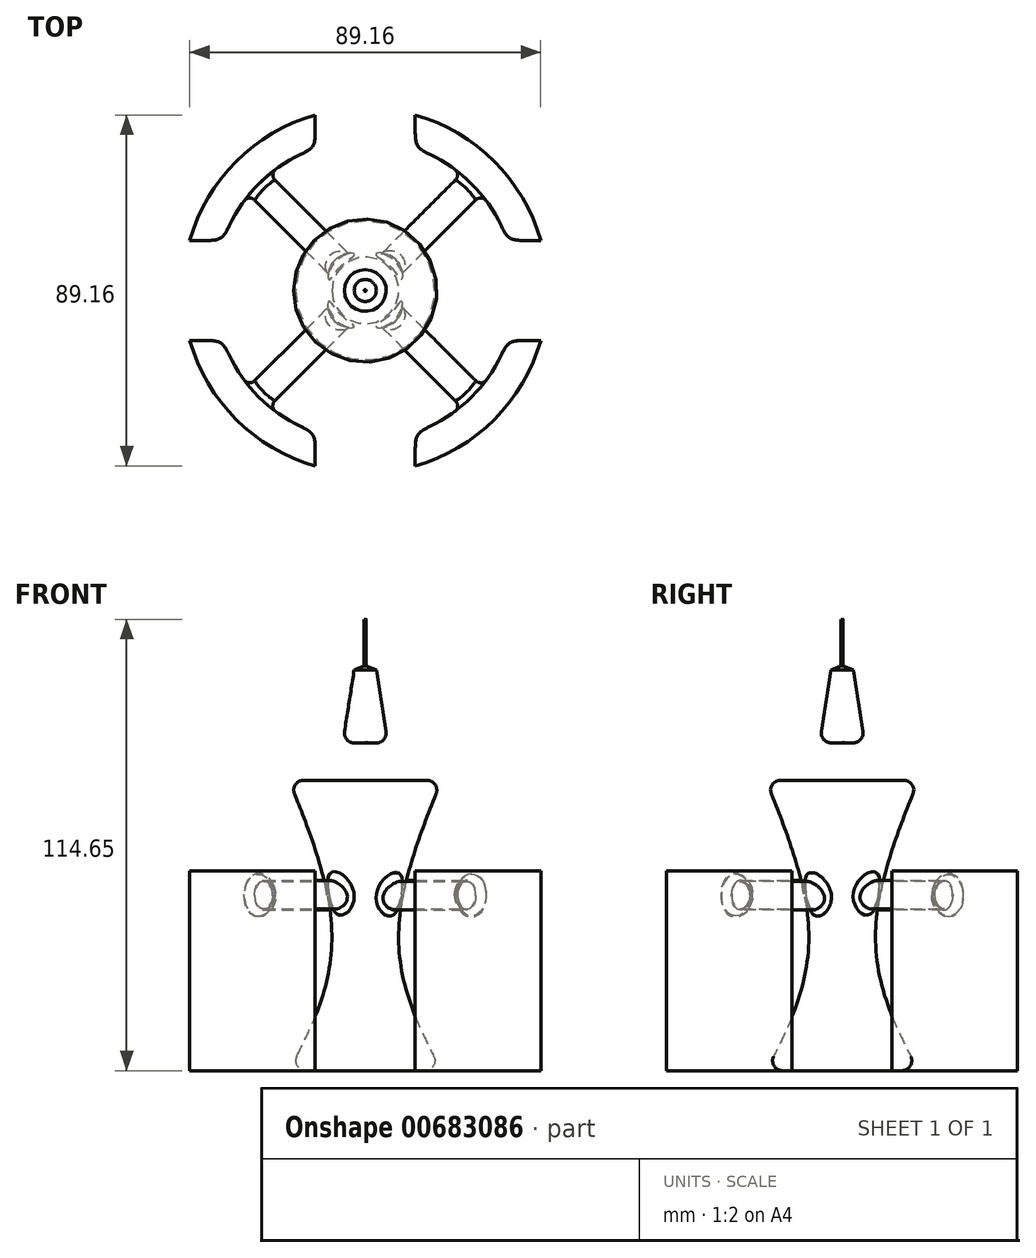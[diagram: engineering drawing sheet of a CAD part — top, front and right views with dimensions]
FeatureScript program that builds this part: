
annotation { "Feature Type Name" : "Feature", "Feature Type Description" : "" }
export const myFeature = defineFeature(function(context is Context, id is Id, definition is map)
    precondition{}
    {
        {
            var Q0;
            Q0=qCreatedBy(makeId("Front.planeOp"),FACE);
            var sketch = newSketch(context, id + "F0", { "sketchPlane" : qUnion([Q0])});
            skLineSegment(sketch, "E0", {"start": v(0, 0) * mm, "end": v(0, 83.5) * mm});
            skLineSegment(sketch, "E1", {"start": v(0, 0) * mm, "end": v(19.3, 0) * mm});
            skFitSpline(sketch, "E2", {"points": [v(19.3, 0) * mm, v(8.76, 39.22) * mm, v(19.3, 73.63) * mm, v(19.3, 73.81) * mm], "startDerivative": vector(-36.92, 71.14) * mm, "endDerivative": vector(-1.25, 3) * mm});
            skFitSpline(sketch, "E3", {"points": [v(19.32, 73.78) * mm, v(0, 83.5) * mm], "startDerivative": vector(-8.92, 8.43) * mm, "endDerivative": vector(-32.32, 1.43) * mm});
            skLineSegment(sketch, "E4", {"start": v(5.85, 82.58) * mm, "end": v(2.8, 101.8) * mm});
            skLineSegment(sketch, "E5", {"start": v(2.8, 101.8) * mm, "end": v(0.25, 102.86) * mm});
            skLineSegment(sketch, "E6", {"start": v(0, 102.96) * mm, "end": v(0, 83.5) * mm});
            skLineSegment(sketch, "E7", {"start": v(0, 102.96) * mm, "end": v(0, 114.65) * mm});
            skLineSegment(sketch, "E8.0", {"start": v(0.25, 102.86) * mm, "end": v(0.25, 114.65) * mm});
            skLineSegment(sketch, "E9", {"start": v(0.25, 114.65) * mm, "end": v(0, 114.65) * mm});
            skLineSegment(sketch, "E10", {"start": v(19.32, 73.78) * mm, "end": v(0, 73.78) * mm});
            skSolve(sketch);
        }
        {
            var Q0;
            {var subQ0=sQuery(id+"F0.wireOp",EDGE,"E0");Q0=makeQuery(id+"F0.imprint","IMPRINT",FACE,{"disambiguationData":[TD([[makeQuery(id+"F0.imprint","IMPRINT",EDGE,{"derivedFrom":subQ0}),-1.0]])]});}
            var Q1;
            {var subQ6=sQuery(id+"F0.wireOp",EDGE,"E6");Q1=makeQuery(id+"F0.imprint","IMPRINT",FACE,{"disambiguationData":[TD([[makeQuery(id+"F0.imprint","IMPRINT",EDGE,{"derivedFrom":subQ6}),1.0]])]});}
            var Q2;
            {var subQ0=sQuery(id+"F0.wireOp",EDGE,"E7");Q2=makeQuery(id+"F0.imprint","IMPRINT",FACE,{"disambiguationData":[TD([[makeQuery(id+"F0.imprint","IMPRINT",EDGE,{"derivedFrom":subQ0}),-1.0]])]});}
            var Q3;
            Q3=sQuery(id+"F0.wireOp",EDGE,"E7");
            revolve(context, id + "F1", {"entities" : qUnion([Q0, Q1, Q2]), "axis" : qUnion([Q3]), "revolveType" : RevolveType.FULL});
        }
        {
            var Q0;
            Q0=makeQuery(id+"F1.opRevolve","SWEPT_EDGE",EDGE,{"disambiguationData":[OSD([sQuery(id+"F0.wireOp",EDGE,"E2"),sQuery(id+"F0.wireOp",EDGE,"E3")])]});
            var Q1;
            Q1=makeQuery(id+"F1.opRevolve","SWEPT_EDGE",EDGE,{"disambiguationData":[OSD([sQuery(id+"F0.wireOp",EDGE,"E3"),sQuery(id+"F0.wireOp",EDGE,"E4")])]});
            fillet(context, id + "F2", {"entities" : qUnion([Q0, Q1]), "radius" : 2.54 * mm, "tangentPropagation" : true, "allowEdgeOverflow" : false});
        }
        {
            var Q0;
            Q0=qCreatedBy(makeId("Top.planeOp"),FACE);
            var sketch = newSketch(context, id + "F3", { "sketchPlane" : qUnion([Q0])});
            skArc(sketch, "E11", {"start": v(-12.7, 44.58) * mm, "mid": v(-32.78, 32.78) * mm, "end": v(-44.58, 12.7) * mm});
            skArc(sketch, "E12", {"start": v(-12.7, 36.1) * mm, "mid": v(-27.06, 27.06) * mm, "end": v(-36.1, 12.7) * mm});
            skArc(sketch, "E13.trimOffspring", {"start": v(-44.58, -12.7) * mm, "mid": v(-32.78, -32.78) * mm, "end": v(-12.7, -44.58) * mm});
            skArc(sketch, "E14.trimOffspring", {"start": v(-36.1, -12.7) * mm, "mid": v(-27.06, -27.06) * mm, "end": v(-12.7, -36.1) * mm});
            skArc(sketch, "E15.trimOffspring", {"start": v(12.7, -36.1) * mm, "mid": v(27.06, -27.06) * mm, "end": v(36.1, -12.7) * mm});
            skArc(sketch, "E16.trimOffspring", {"start": v(12.7, -44.58) * mm, "mid": v(32.78, -32.78) * mm, "end": v(44.58, -12.7) * mm});
            skArc(sketch, "E17.trimOffspring", {"start": v(36.1, 12.7) * mm, "mid": v(27.06, 27.06) * mm, "end": v(12.7, 36.1) * mm});
            skArc(sketch, "E18.trimOffspring", {"start": v(44.58, 12.7) * mm, "mid": v(32.78, 32.78) * mm, "end": v(12.7, 44.58) * mm});
            skLineSegment(sketch, "E19.0", {"start": v(36.1, 12.7) * mm, "end": v(44.58, 12.7) * mm});
            skLineSegment(sketch, "E20.0", {"start": v(36.1, -12.7) * mm, "end": v(44.58, -12.7) * mm});
            skLineSegment(sketch, "E21.0", {"start": v(-12.7, 36.1) * mm, "end": v(-12.7, 44.58) * mm});
            skLineSegment(sketch, "E22.0", {"start": v(12.7, 36.1) * mm, "end": v(12.7, 44.58) * mm});
            skLineSegment(sketch, "E23.0", {"start": v(-36.1, -12.7) * mm, "end": v(-44.58, -12.7) * mm});
            skLineSegment(sketch, "E24.0", {"start": v(-36.1, 12.7) * mm, "end": v(-44.58, 12.7) * mm});
            skLineSegment(sketch, "E25.0", {"start": v(12.7, -36.1) * mm, "end": v(12.7, -44.58) * mm});
            skLineSegment(sketch, "E26.0", {"start": v(-12.7, -36.1) * mm, "end": v(-12.7, -44.58) * mm});
            skSolve(sketch);
        }
        {
            var Q0;
            Q0=makeQuery(id+"F3.imprint","IMPRINT",FACE,{"disambiguationData":[TD([[makeQuery(id+"F3.imprint","IMPRINT",EDGE,{"derivedFrom":sQuery(id+"F3.wireOp",EDGE,"E11")}),1.0]])]});
            var Q1;
            Q1=makeQuery(id+"F3.imprint","IMPRINT",FACE,{"disambiguationData":[TD([[makeQuery(id+"F3.imprint","IMPRINT",EDGE,{"derivedFrom":sQuery(id+"F3.wireOp",EDGE,"E13.trimOffspring")}),1.0]])]});
            var Q2;
            Q2=makeQuery(id+"F3.imprint","IMPRINT",FACE,{"disambiguationData":[TD([[makeQuery(id+"F3.imprint","IMPRINT",EDGE,{"derivedFrom":sQuery(id+"F3.wireOp",EDGE,"E15.trimOffspring")}),-1.0]])]});
            var Q3;
            Q3=makeQuery(id+"F3.imprint","IMPRINT",FACE,{"disambiguationData":[TD([[makeQuery(id+"F3.imprint","IMPRINT",EDGE,{"derivedFrom":sQuery(id+"F3.wireOp",EDGE,"E17.trimOffspring")}),-1.0]])]});
            extrude(context, id + "F4", {"entities" : qUnion([Q0, Q1, Q2, Q3]), "depth" : 50.8 * mm, "offsetDistance" : 25.4 * mm});
        }
        {
            var Q0;
            Q0=makeQuery(id+"F4.opExtrude","CAP_FACE",FACE,{"disambiguationData":[OSD([sQuery(id+"F3.wireOp",EDGE,"E15.trimOffspring"),sQuery(id+"F3.wireOp",EDGE,"E16.trimOffspring"),sQuery(id+"F3.wireOp",EDGE,"E20.0"),sQuery(id+"F3.wireOp",EDGE,"E25.0")])],"isStart":false});
            cPlane(context, id + "F5", {"entities" : qUnion([Q0]), "cplaneType" : CPlaneType.OFFSET, "offset" : 6.35 * mm, "oppositeDirection" : true, "width" : 152.4 * mm, "height" : 152.4 * mm});
        }
        {
            var Q0;
            Q0=qCreatedBy(id+"F5.planeOp",FACE);
            var sketch = newSketch(context, id + "F6", { "sketchPlane" : qUnion([Q0])});
            skArc(sketch, "E27.0", {"start": v(12.7, -36.1) * mm, "mid": v(27.06, -27.06) * mm, "end": v(36.1, -12.7) * mm});
            skLineSegment(sketch, "E28.0.0", {"start": v(12.7, -36.1) * mm, "end": v(12.7, -44.58) * mm});
            skArc(sketch, "E28.0.1", {"start": v(12.7, -44.58) * mm, "mid": v(32.78, -32.78) * mm, "end": v(44.58, -12.7) * mm});
            skLineSegment(sketch, "E28.0.2", {"start": v(44.58, -12.7) * mm, "end": v(36.1, -12.7) * mm});
            skArc(sketch, "E28.0.3", {"start": v(36.1, -12.7) * mm, "mid": v(27.06, -27.06) * mm, "end": v(12.7, -36.1) * mm});
            skArc(sketch, "E29.0", {"start": v(-36.1, -12.7) * mm, "mid": v(-27.06, -27.06) * mm, "end": v(-12.7, -36.1) * mm});
            skLineSegment(sketch, "E30.0.0", {"start": v(36.1, 12.7) * mm, "end": v(44.58, 12.7) * mm});
            skArc(sketch, "E30.0.1", {"start": v(44.58, 12.7) * mm, "mid": v(32.78, 32.78) * mm, "end": v(12.7, 44.58) * mm});
            skLineSegment(sketch, "E30.0.2", {"start": v(12.7, 44.58) * mm, "end": v(12.7, 36.1) * mm});
            skArc(sketch, "E30.0.3", {"start": v(12.7, 36.1) * mm, "mid": v(27.06, 27.06) * mm, "end": v(36.1, 12.7) * mm});
            skArc(sketch, "E31.0.0", {"start": v(-36.1, 12.7) * mm, "mid": v(-27.06, 27.06) * mm, "end": v(-12.7, 36.1) * mm});
            skLineSegment(sketch, "E31.0.1", {"start": v(-12.7, 36.1) * mm, "end": v(-12.7, 44.58) * mm});
            skArc(sketch, "E31.0.2", {"start": v(-12.7, 44.58) * mm, "mid": v(-32.78, 32.78) * mm, "end": v(-44.58, 12.7) * mm});
            skLineSegment(sketch, "E31.0.3", {"start": v(-44.58, 12.7) * mm, "end": v(-36.1, 12.7) * mm});
            skLineSegment(sketch, "E32", {"start": v(27.06, -27.06) * mm, "end": v(0, 0) * mm});
            skLineSegment(sketch, "E33", {"start": v(27.06, 27.06) * mm, "end": v(0, 0) * mm});
            skLineSegment(sketch, "E34", {"start": v(-27.06, 27.06) * mm, "end": v(0, 0) * mm});
            skLineSegment(sketch, "E35", {"start": v(-27.06, -27.06) * mm, "end": v(0, 0) * mm});
            skSolve(sketch);
        }
        {
            var Q0;
            Q0=sQuery(id+"F6.wireOp",EDGE,"E31.0.0");
            cPoint(context, id + "F7", {"entities" : qUnion([Q0]), "parameter" : 0.5});
        }
        {
            var Q0;
            Q0 = qCreatedBy(id + "F7" ,VERTEX);
            var Q1;
            Q1=sQuery(id+"F6.wireOp",EDGE,"E34");
            cPlane(context, id + "F8", {"entities" : qUnion([Q0, Q1]), "cplaneType" : CPlaneType.LINE_POINT, "offset" : 25.4 * mm, "width" : 152.4 * mm, "height" : 152.4 * mm});
        }
        {
            var Q0;
            Q0=qCreatedBy(id+"F8.planeOp",FACE);
            var sketch = newSketch(context, id + "F9", { "sketchPlane" : qUnion([Q0])});
            skPoint(sketch, "E36.0", {"position": v(0, 44.45) * mm});
            skCircle(sketch, "E37", {"center": v(0, 44.45) * mm, "radius": 3.62 * mm});
            skSolve(sketch);
        }
        {
            var Q0;
            Q0=makeQuery(id+"F9.imprint","IMPRINT",FACE,{"disambiguationData":[TD([[makeQuery(id+"F9.imprint","IMPRINT",EDGE,{"derivedFrom":sQuery(id+"F9.wireOp",EDGE,"E37")}),1.0]])]});
            var Q1;
            Q1=sQuery(id+"F6.wireOp",EDGE,"E34");
            var Q2;
            Q2=sQuery(id+"F6.wireOp",EDGE,"E32");
            sweep(context, id + "F10", {"operationType" : NewBodyOperationType.ADD, "profiles" : qUnion([Q0]), "path" : qUnion([Q1, Q2])});
        }
        {
            var Q0;
            Q0=sQuery(id+"F6.wireOp",VERTEX,"E35.start");
            var Q1;
            Q1=sQuery(id+"F6.wireOp",EDGE,"E35");
            cPlane(context, id + "F11", {"entities" : qUnion([Q0, Q1]), "cplaneType" : CPlaneType.CURVE_POINT, "offset" : 25.4 * mm, "width" : 152.4 * mm, "height" : 152.4 * mm});
        }
        {
            var Q0;
            Q0=qCreatedBy(id+"F11.planeOp",FACE);
            var sketch = newSketch(context, id + "F12", { "sketchPlane" : qUnion([Q0])});
            skCircle(sketch, "E38", {"center": v(0.04, 44.72) * mm, "radius": 3.62 * mm});
            skSolve(sketch);
        }
        {
            var Q0;
            Q0=makeQuery(id+"F12.imprint","IMPRINT",FACE,{"disambiguationData":[TD([[makeQuery(id+"F12.imprint","IMPRINT",EDGE,{"derivedFrom":sQuery(id+"F12.wireOp",EDGE,"E38")}),1.0]])]});
            var Q1;
            Q1=sQuery(id+"F6.wireOp",EDGE,"E35");
            var Q2;
            Q2=sQuery(id+"F6.wireOp",EDGE,"E33");
            sweep(context, id + "F13", {"operationType" : NewBodyOperationType.ADD, "profiles" : qUnion([Q0]), "path" : qUnion([Q1, Q2])});
        }
        {
            var Q0;
            Q0=makeQuery(id+"F13.boolean.opBoolean","INTERSECT",EDGE,{"derivedFrom":[makeQuery(id+"F4.opExtrude","SWEPT_FACE",FACE,{"disambiguationData":[OSD([sQuery(id+"F3.wireOp",EDGE,"E17.trimOffspring")])]}),makeQuery(id+"F13.opSweep","SWEPT_FACE",FACE,{"disambiguationData":[OSD([sQuery(id+"F6.wireOp",EDGE,"E35"),sQuery(id+"F12.wireOp",EDGE,"E38")])]})]});
            var Q1;
            Q1=makeQuery(id+"F10.boolean.opBoolean","INTERSECT",EDGE,{"derivedFrom":[makeQuery(id+"F4.opExtrude","SWEPT_FACE",FACE,{"disambiguationData":[OSD([sQuery(id+"F3.wireOp",EDGE,"E12")])]}),makeQuery(id+"F10.opSweep","SWEPT_FACE",FACE,{"disambiguationData":[OSD([sQuery(id+"F6.wireOp",EDGE,"E34"),sQuery(id+"F9.wireOp",EDGE,"E37")])]})]});
            var Q2;
            Q2=makeQuery(id+"F10.boolean.opBoolean","INTERSECT",EDGE,{"disambiguationData":[OD(0.0)],"derivedFrom":[makeQuery(id+"F1.opRevolve","SWEPT_FACE",FACE,{"disambiguationData":[OSD([sQuery(id+"F0.wireOp",EDGE,"E2")])]}),makeQuery(id+"F10.opSweep","SWEPT_FACE",FACE,{"disambiguationData":[OSD([sQuery(id+"F6.wireOp",EDGE,"E34"),sQuery(id+"F9.wireOp",EDGE,"E37")])]})]});
            var Q3;
            Q3=makeQuery(id+"F13.boolean.opBoolean","INTERSECT",EDGE,{"disambiguationData":[OD(0.0)],"derivedFrom":[makeQuery(id+"F1.opRevolve","SWEPT_FACE",FACE,{"disambiguationData":[OSD([sQuery(id+"F0.wireOp",EDGE,"E2")])]}),makeQuery(id+"F13.opSweep","SWEPT_FACE",FACE,{"disambiguationData":[OSD([sQuery(id+"F6.wireOp",EDGE,"E35"),sQuery(id+"F12.wireOp",EDGE,"E38")])]})]});
            var Q4;
            Q4=makeQuery(id+"F10.boolean.opBoolean","INTERSECT",EDGE,{"disambiguationData":[OD(1.0)],"derivedFrom":[makeQuery(id+"F1.opRevolve","SWEPT_FACE",FACE,{"disambiguationData":[OSD([sQuery(id+"F0.wireOp",EDGE,"E2")])]}),makeQuery(id+"F10.opSweep","SWEPT_FACE",FACE,{"disambiguationData":[OSD([sQuery(id+"F6.wireOp",EDGE,"E34"),sQuery(id+"F9.wireOp",EDGE,"E37")])]})]});
            var Q5;
            Q5=makeQuery(id+"F10.boolean.opBoolean","INTERSECT",EDGE,{"derivedFrom":[makeQuery(id+"F4.opExtrude","SWEPT_FACE",FACE,{"disambiguationData":[OSD([sQuery(id+"F3.wireOp",EDGE,"E15.trimOffspring")])]}),makeQuery(id+"F10.opSweep","SWEPT_FACE",FACE,{"disambiguationData":[OSD([sQuery(id+"F6.wireOp",EDGE,"E34"),sQuery(id+"F9.wireOp",EDGE,"E37")])]})]});
            var Q6;
            Q6=makeQuery(id+"F13.boolean.opBoolean","INTERSECT",EDGE,{"derivedFrom":[makeQuery(id+"F4.opExtrude","SWEPT_FACE",FACE,{"disambiguationData":[OSD([sQuery(id+"F3.wireOp",EDGE,"E14.trimOffspring")])]}),makeQuery(id+"F13.opSweep","SWEPT_FACE",FACE,{"disambiguationData":[OSD([sQuery(id+"F6.wireOp",EDGE,"E35"),sQuery(id+"F12.wireOp",EDGE,"E38")])]})]});
            var Q7;
            Q7=makeQuery(id+"F13.boolean.opBoolean","INTERSECT",EDGE,{"disambiguationData":[OD(1.0)],"derivedFrom":[makeQuery(id+"F1.opRevolve","SWEPT_FACE",FACE,{"disambiguationData":[OSD([sQuery(id+"F0.wireOp",EDGE,"E2")])]}),makeQuery(id+"F13.opSweep","SWEPT_FACE",FACE,{"disambiguationData":[OSD([sQuery(id+"F6.wireOp",EDGE,"E35"),sQuery(id+"F12.wireOp",EDGE,"E38")])]})]});
            fillet(context, id + "F14", {"entities" : qUnion([Q0, Q1, Q2, Q3, Q4, Q5, Q6, Q7]), "radius" : 1.78 * mm, "tangentPropagation" : true, "allowEdgeOverflow" : false});
        }
        {
            var Q0;
            Q0=makeQuery(id+"F4.opExtrude","SWEPT_EDGE",EDGE,{"disambiguationData":[OSD([sQuery(id+"F3.wireOp",EDGE,"E15.trimOffspring"),sQuery(id+"F3.wireOp",EDGE,"E20.0")])]});
            var Q1;
            Q1=makeQuery(id+"F4.opExtrude","SWEPT_EDGE",EDGE,{"disambiguationData":[OSD([sQuery(id+"F3.wireOp",EDGE,"E15.trimOffspring"),sQuery(id+"F3.wireOp",EDGE,"E25.0")])]});
            var Q2;
            Q2=makeQuery(id+"F4.opExtrude","SWEPT_EDGE",EDGE,{"disambiguationData":[OSD([sQuery(id+"F3.wireOp",EDGE,"E14.trimOffspring"),sQuery(id+"F3.wireOp",EDGE,"E26.0")])]});
            var Q3;
            Q3=makeQuery(id+"F4.opExtrude","SWEPT_EDGE",EDGE,{"disambiguationData":[OSD([sQuery(id+"F3.wireOp",EDGE,"E14.trimOffspring"),sQuery(id+"F3.wireOp",EDGE,"E23.0")])]});
            var Q4;
            Q4=makeQuery(id+"F4.opExtrude","SWEPT_EDGE",EDGE,{"disambiguationData":[OSD([sQuery(id+"F3.wireOp",EDGE,"E12"),sQuery(id+"F3.wireOp",EDGE,"E21.0")])]});
            var Q5;
            Q5=makeQuery(id+"F4.opExtrude","SWEPT_EDGE",EDGE,{"disambiguationData":[OSD([sQuery(id+"F3.wireOp",EDGE,"E12"),sQuery(id+"F3.wireOp",EDGE,"E24.0")])]});
            var Q6;
            Q6=makeQuery(id+"F4.opExtrude","SWEPT_EDGE",EDGE,{"disambiguationData":[OSD([sQuery(id+"F3.wireOp",EDGE,"E17.trimOffspring"),sQuery(id+"F3.wireOp",EDGE,"E19.0")])]});
            var Q7;
            Q7=makeQuery(id+"F4.opExtrude","SWEPT_EDGE",EDGE,{"disambiguationData":[OSD([sQuery(id+"F3.wireOp",EDGE,"E17.trimOffspring"),sQuery(id+"F3.wireOp",EDGE,"E22.0")])]});
            fillet(context, id + "F15", {"entities" : qUnion([Q0, Q1, Q2, Q3, Q4, Q5, Q6, Q7]), "radius" : 6.35 * mm, "tangentPropagation" : true, "rho" : .65, "crossSection" : FilletCrossSection.CONIC, "allowEdgeOverflow" : false});
        }
    });
